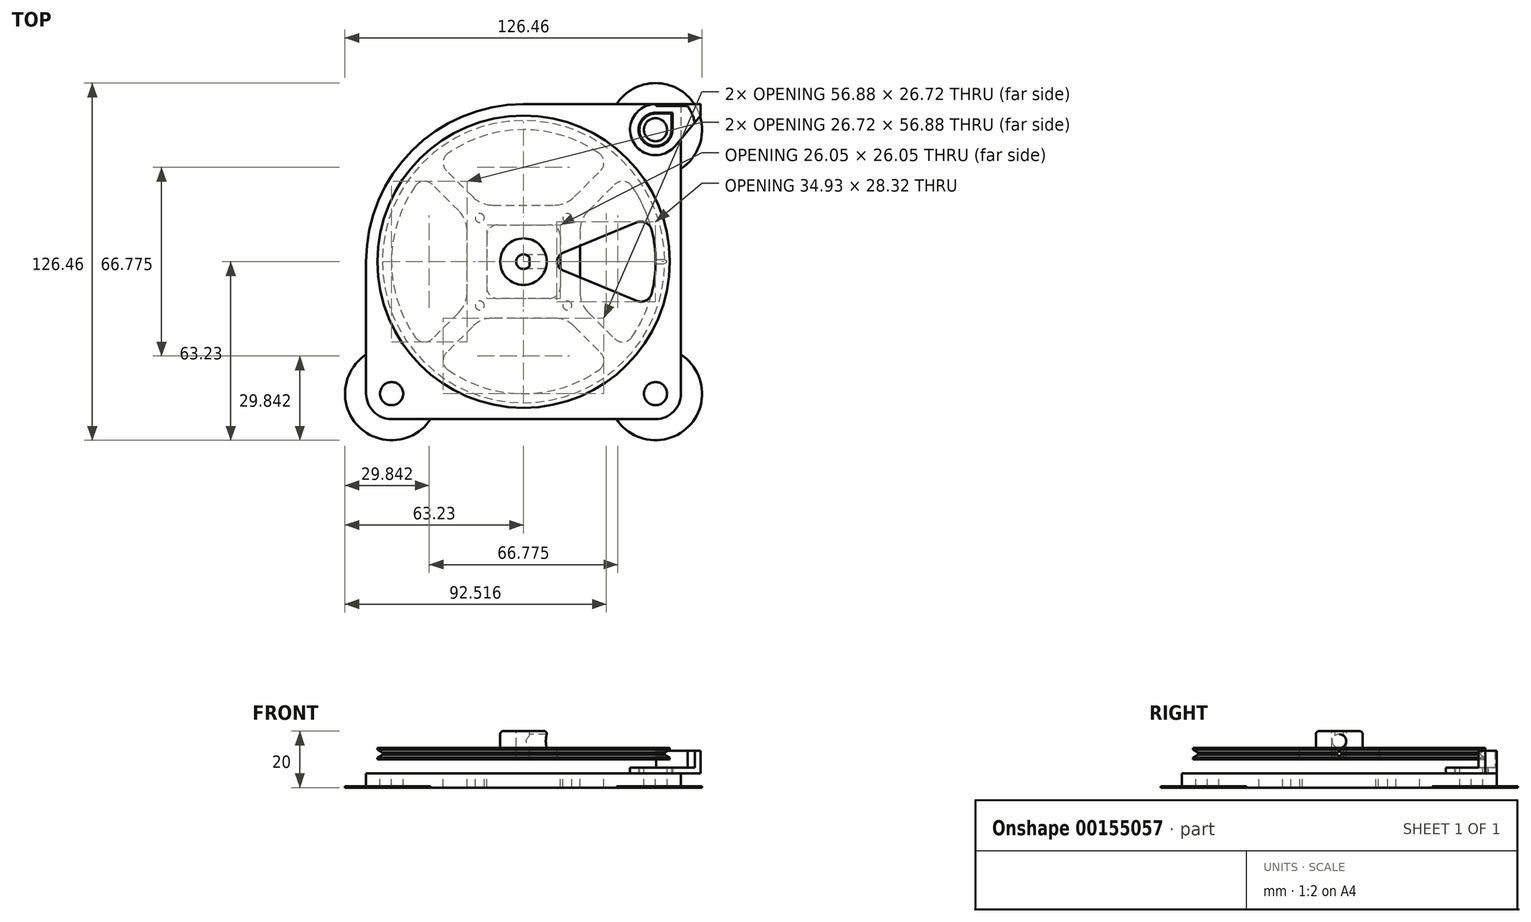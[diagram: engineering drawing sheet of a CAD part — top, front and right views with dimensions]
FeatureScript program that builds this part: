
annotation { "Feature Type Name" : "Feature", "Feature Type Description" : "" }
export const myFeature = defineFeature(function(context is Context, id is Id, definition is map)
    precondition{}
    {
        {
            var Q0;
            Q0=qCreatedBy(makeId("Top.planeOp"),FACE);
            var sketch = newSketch(context, id + "F0", { "sketchPlane" : qUnion([Q0])});
            skCircle(sketch, "E0", {"center": v(0, 0) * mm, "radius": 51.75 * mm});
            skSolve(sketch);
        }
        {
            var Q0;
            Q0 = qSketchRegion(id + "F0", true);
            extrude(context, id + "F1", {"entities" : qUnion([Q0]), "depth" : 4 * mm});
        }
        {
            var Q0;
            Q0=qCreatedBy(makeId("Front.planeOp"),FACE);
            var sketch = newSketch(context, id + "F2", { "sketchPlane" : qUnion([Q0])});
            skPoint(sketch, "E1", {"position": v(35.4, 14.63) * mm});
            skLineSegment(sketch, "E2", {"start": v(51.75, 3.4) * mm, "end": v(51.75, 0.6) * mm});
            skLineSegment(sketch, "E3", {"start": v(51.75, 3.4) * mm, "end": v(51.75, 0.6) * mm, "construction": true});
            skPoint(sketch, "E4", {"position": v(51.75, 2) * mm});
            skLineSegment(sketch, "E5", {"start": v(51.75, 3.4) * mm, "end": v(50, 2.39) * mm});
            skLineSegment(sketch, "E6", {"start": v(50, 2.39) * mm, "end": v(50, 1.61) * mm});
            skLineSegment(sketch, "E7", {"start": v(50, 1.61) * mm, "end": v(51.75, 0.6) * mm});
            skLineSegment(sketch, "E8", {"start": v(51.75, 0.6) * mm, "end": v(51.75, 3.4) * mm});
            skPoint(sketch, "E9", {"position": v(50, 2) * mm});
            skPoint(sketch, "E10.orphan", {"position": v(51.75, 4) * mm});
            skPoint(sketch, "E11.orphan", {"position": v(51.75, 0) * mm});
            skSolve(sketch);
        }
        {
            var Q0;
            Q0 = qSketchRegion(id + "F2", true);
            var Q1;
            Q1=makeQuery(id+"F1.opExtrude","CAP_EDGE",EDGE,{"disambiguationData":[OSD([sQuery(id+"F0.wireOp",EDGE,"E0")])],"isStart":false});
            revolve(context, id + "F3", {"operationType" : NewBodyOperationType.REMOVE, "entities" : qUnion([Q0]), "axis" : qUnion([Q1]), "revolveType" : RevolveType.FULL, "oppositeDirection" : true});
        }
        {
            var Q0;
            Q0=qCreatedBy(makeId("Top.planeOp"),FACE);
            var sketch = newSketch(context, id + "F4", { "sketchPlane" : qUnion([Q0])});
            skArc(sketch, "E12", {"start": v(2.09, 1.55) * mm, "mid": v(-2.6, 0) * mm, "end": v(2.09, -1.55) * mm});
            skLineSegment(sketch, "E13", {"start": v(2.1, 1.55) * mm, "end": v(2.1, -1.55) * mm});
            skSolve(sketch);
        }
        {
            var Q0;
            Q0=makeQuery(id+"F1.opExtrude","CAP_FACE",FACE,{"disambiguationData":[OSD([sQuery(id+"F0.wireOp",EDGE,"E0")])],"isStart":false});
            var sketch = newSketch(context, id + "F5", { "sketchPlane" : qUnion([Q0])});
            skArc(sketch, "E14", {"start": v(13.85, 3.03) * mm, "mid": v(11.82, 0) * mm, "end": v(13.85, -3.03) * mm});
            skLineSegment(sketch, "E15", {"start": v(13.85, 3.03) * mm, "end": v(40, 13.86) * mm});
            skLineSegment(sketch, "E16", {"start": v(13.85, -3.03) * mm, "end": v(40, -13.86) * mm});
            skLineSegment(sketch, "E17", {"start": v(0, 0) * mm, "end": v(33.6, 13.92) * mm, "construction": true});
            skArc(sketch, "E18", {"start": v(45.4, -11.12) * mm, "mid": v(46.75, 0) * mm, "end": v(45.4, 11.12) * mm});
            skPoint(sketch, "E19.visualSharp", {"position": v(44.09, 15.56) * mm});
            skArc(sketch, "E19.filletArc", {"start": v(45.4, 11.12) * mm, "mid": v(43.33, 13.73) * mm, "end": v(40, 13.86) * mm});
            skPoint(sketch, "E20.visualSharp", {"position": v(44.09, -15.56) * mm});
            skArc(sketch, "E20.filletArc", {"start": v(40, -13.86) * mm, "mid": v(43.33, -13.73) * mm, "end": v(45.4, -11.12) * mm});
            skSolve(sketch);
        }
        {
            var Q0;
            Q0 = qSketchRegion(id + "F5", true);
            extrude(context, id + "F6", {"entities" : qUnion([Q0]), "operationType" : NewBodyOperationType.REMOVE, "endBound" : BoundingType.SYMMETRIC, "depth" : 25 * mm});
        }
        {
            var Q0;
            Q0 = qSketchRegion(id + "F4", true);
            extrude(context, id + "F7", {"entities" : qUnion([Q0]), "operationType" : NewBodyOperationType.REMOVE, "endBound" : BoundingType.SYMMETRIC, "oppositeDirection" : true, "depth" : 25 * mm});
        }
        {
            var Q0;
            Q0=makeQuery(id+"F1.opExtrude","CAP_FACE",FACE,{"disambiguationData":[OSD([sQuery(id+"F0.wireOp",EDGE,"E0")])],"isStart":false});
            var sketch = newSketch(context, id + "F8", { "sketchPlane" : qUnion([Q0])});
            skCircle(sketch, "E21", {"center": v(0, 0) * mm, "radius": 8.25 * mm});
            skArc(sketch, "E22.0", {"start": v(2.09, 1.55) * mm, "mid": v(-2.6, 0) * mm, "end": v(2.09, -1.55) * mm});
            skLineSegment(sketch, "E23.0", {"start": v(2.1, 1.55) * mm, "end": v(2.1, -1.55) * mm});
            skSolve(sketch);
        }
        {
            var Q0;
            Q0 = qSketchRegion(id + "F8", true);
            extrude(context, id + "F9", {"entities" : qUnion([Q0]), "operationType" : NewBodyOperationType.ADD, "depth" : 6 * mm});
        }
        {
            var Q0;
            Q0=makeQuery(id+"F9.opExtrude","CAP_EDGE",EDGE,{"disambiguationData":[OSD([sQuery(id+"F8.wireOp",EDGE,"E21")])],"isStart":true});
            var Q1;
            Q1=makeQuery(id+"F9.opExtrude","CAP_EDGE",EDGE,{"disambiguationData":[OSD([sQuery(id+"F8.wireOp",EDGE,"E21")])],"isStart":false});
            fillet(context, id + "F10", {"entities" : qUnion([Q0, Q1]), "radius" : 1 * mm, "tangentPropagation" : true, "allowEdgeOverflow" : false});
        }
        {
            var Q0;
            Q0=qCreatedBy(makeId("Right.planeOp"),FACE);
            var sketch = newSketch(context, id + "F11", { "sketchPlane" : qUnion([Q0])});
            skCircle(sketch, "E24", {"center": v(0, 6.45) * mm, "radius": 2.45 * mm});
            skLineSegment(sketch, "E25", {"start": v(-8.25, 5.5) * mm, "end": v(-8.25, 7.4) * mm, "construction": true});
            skLineSegment(sketch, "E26", {"start": v(8.25, 8.5) * mm, "end": v(8.25, 5.5) * mm});
            skPoint(sketch, "E27", {"position": v(-8.25, 6.45) * mm});
            skSolve(sketch);
        }
        {
            var Q0;
            Q0 = qSketchRegion(id + "F11", true);
            extrude(context, id + "F12", {"entities" : qUnion([Q0]), "operationType" : NewBodyOperationType.REMOVE, "depth" : 25 * mm});
        }
        {
            var Q0;
            Q0=qCreatedBy(makeId("Right.planeOp"),FACE);
            var Q1;
            Q1=sQuery(id+"F2.wireOp",VERTEX,"E4");
            cPlane(context, id + "F13", {"entities" : qUnion([Q0, Q1]), "cplaneType" : CPlaneType.PLANE_POINT, "offset" : 25 * mm, "width" : 150 * mm, "height" : 150 * mm});
        }
        {
            var Q0;
            Q0=qCreatedBy(id+"F13.planeOp",FACE);
            var sketch = newSketch(context, id + "F14", { "sketchPlane" : qUnion([Q0])});
            skPoint(sketch, "E28.0", {"position": v(0, 2) * mm});
            skCircle(sketch, "E29", {"center": v(0, 2) * mm, "radius": 0.75 * mm});
            skSolve(sketch);
        }
        {
            var Q0;
            Q0 = qSketchRegion(id + "F14", true);
            var Q1;
            Q1=makeQuery(id+"F6.boolean.opBoolean","COPY",FACE,{"derivedFrom":makeQuery(id+"F6.opExtrude","SWEPT_FACE",FACE,{"disambiguationData":[OSD([sQuery(id+"F5.wireOp",EDGE,"E18")])]})});
            extrude(context, id + "F15", {"entities" : qUnion([Q0]), "operationType" : NewBodyOperationType.REMOVE, "endBound" : BoundingType.UP_TO_SURFACE, "oppositeDirection" : true, "endBoundEntityFace" : qUnion([Q1]), "depth" : 25 * mm});
        }
        {
            var Q0;
            Q0=qCreatedBy(makeId("Top.planeOp"),FACE);
            cPlane(context, id + "F16", {"entities" : qUnion([Q0]), "cplaneType" : CPlaneType.OFFSET, "offset" : 5 * mm, "oppositeDirection" : true, "width" : 150 * mm, "height" : 150 * mm});
        }
        {
            var Q0;
            Q0=qCreatedBy(id+"F16.planeOp",FACE);
            var sketch = newSketch(context, id + "F17", { "sketchPlane" : qUnion([Q0])});
            skArc(sketch, "E30.0", {"start": v(2.09, 1.55) * mm, "mid": v(-2.6, 0) * mm, "end": v(2.09, -1.55) * mm});
            skCircle(sketch, "E31", {"center": v(0, 0) * mm, "radius": 2.8 * mm});
            skLineSegment(sketch, "E32.bottom", {"start": v(0, 55.75) * mm, "end": v(46.73, 55.75) * mm});
            skLineSegment(sketch, "E32.top", {"start": v(-46.73, -55.75) * mm, "end": v(46.73, -55.75) * mm});
            skLineSegment(sketch, "E32.left", {"start": v(-55.75, 0) * mm, "end": v(-55.75, -46.73) * mm});
            skLineSegment(sketch, "E32.right", {"start": v(55.75, 55.75) * mm, "end": v(55.75, -46.73) * mm});
            skCircle(sketch, "E33.0", {"center": v(0, 0) * mm, "radius": 51.75 * mm, "construction": true});
            skPoint(sketch, "E34", {"position": v(-55.75, 0) * mm});
            skPoint(sketch, "E35", {"position": v(0, -55.75) * mm});
            skCircle(sketch, "E36", {"center": v(-46.73, -46.73) * mm, "radius": 4.1 * mm});
            skArc(sketch, "E37", {"start": v(-55.75, -46.73) * mm, "mid": v(-53.1, -53.1) * mm, "end": v(-46.73, -55.75) * mm});
            skArc(sketch, "E38.1.0.0", {"start": v(46.73, -55.75) * mm, "mid": v(53.1, -53.1) * mm, "end": v(55.75, -46.73) * mm});
            skCircle(sketch, "E38.1.0.1", {"center": v(46.73, -46.73) * mm, "radius": 4.1 * mm});
            skLineSegment(sketch, "E38.direction1", {"start": v(-46.73, -46.73) * mm, "end": v(46.73, -46.73) * mm, "construction": true});
            skArc(sketch, "E39.0.1.0", {"start": v(55.75, 46.73) * mm, "mid": v(53.1, 53.1) * mm, "end": v(46.73, 55.75) * mm, "construction": true});
            skCircle(sketch, "E39.0.1.1", {"center": v(46.73, 46.73) * mm, "radius": 4.1 * mm});
            skLineSegment(sketch, "E39.direction2", {"start": v(46.73, -46.73) * mm, "end": v(46.73, 46.73) * mm, "construction": true});
            skPoint(sketch, "E40.orphan", {"position": v(55.75, -55.75) * mm});
            skPoint(sketch, "E41.orphan", {"position": v(-55.75, -55.75) * mm});
            skCircle(sketch, "E42", {"center": v(0, 0) * mm, "radius": 55.75 * mm});
            skPoint(sketch, "E43.orphan", {"position": v(-55.75, 55.75) * mm});
            skArc(sketch, "E44", {"start": v(58.68, 46.73) * mm, "mid": v(57.6, 51.69) * mm, "end": v(54.57, 55.75) * mm, "construction": true});
            skLineSegment(sketch, "E45", {"start": v(58.68, 46.73) * mm, "end": v(58.68, 55.75) * mm, "construction": true});
            skLineSegment(sketch, "E46.trimOffspring", {"start": v(54.57, 55.75) * mm, "end": v(58.68, 55.75) * mm, "construction": true});
            skLineSegment(sketch, "E47.bottom", {"start": v(46.73, 55.75) * mm, "end": v(55.75, 55.75) * mm});
            skLineSegment(sketch, "E47.right", {"start": v(62.68, 55.75) * mm, "end": v(62.68, 53.75) * mm, "construction": true});
            skLineSegment(sketch, "E48.trimOffspring", {"start": v(55.75, 53.75) * mm, "end": v(62.68, 53.75) * mm, "construction": true});
            skLineSegment(sketch, "E49", {"start": v(55.75, 55.75) * mm, "end": v(62.68, 55.75) * mm, "construction": true});
            skSolve(sketch);
        }
        {
            var Q0;
            Q0 = qSketchRegion(id + "F17", true);
            extrude(context, id + "F18", {"entities" : qUnion([Q0]), "oppositeDirection" : true, "depth" : 5 * mm});
        }
        {
            var Q0;
            Q0=makeQuery(id+"F18.opExtrude","CAP_FACE",FACE,{"disambiguationData":[OSD([sQuery(id+"F17.wireOp",EDGE,"E31"),sQuery(id+"F17.wireOp",EDGE,"E32.bottom"),sQuery(id+"F17.wireOp",EDGE,"E32.top"),sQuery(id+"F17.wireOp",EDGE,"E32.left"),sQuery(id+"F17.wireOp",EDGE,"E32.right"),sQuery(id+"F17.wireOp",EDGE,"E36"),sQuery(id+"F17.wireOp",EDGE,"E37"),sQuery(id+"F17.wireOp",EDGE,"E38.1.0.0"),sQuery(id+"F17.wireOp",EDGE,"E38.1.0.1"),sQuery(id+"F17.wireOp",EDGE,"E39.0.1.0"),sQuery(id+"F17.wireOp",EDGE,"E39.0.1.1"),sQuery(id+"F17.wireOp",EDGE,"E42")])],"isStart":true});
            var sketch = newSketch(context, id + "F19", { "sketchPlane" : qUnion([Q0])});
            skLineSegment(sketch, "E50.bottom", {"start": v(-21.5, 21.75) * mm, "end": v(21.5, 21.75) * mm, "construction": true});
            skLineSegment(sketch, "E50.top", {"start": v(-21.5, -21.75) * mm, "end": v(21.5, -21.75) * mm, "construction": true});
            skLineSegment(sketch, "E50.left", {"start": v(-21.5, 21.75) * mm, "end": v(-21.5, -21.75) * mm, "construction": true});
            skLineSegment(sketch, "E50.right", {"start": v(21.5, 21.75) * mm, "end": v(21.5, -21.75) * mm, "construction": true});
            skLineSegment(sketch, "E51.bottom", {"start": v(-15.5, 15.5) * mm, "end": v(15.5, 15.5) * mm, "construction": true});
            skLineSegment(sketch, "E51.top", {"start": v(-15.5, -15.5) * mm, "end": v(15.5, -15.5) * mm, "construction": true});
            skLineSegment(sketch, "E51.left", {"start": v(-15.5, 15.5) * mm, "end": v(-15.5, -15.5) * mm, "construction": true});
            skLineSegment(sketch, "E51.right", {"start": v(15.5, 15.5) * mm, "end": v(15.5, -15.5) * mm, "construction": true});
            skPoint(sketch, "E52", {"position": v(-21.5, 0) * mm});
            skPoint(sketch, "E53", {"position": v(-15.5, 0) * mm});
            skPoint(sketch, "E54", {"position": v(0, 15.5) * mm});
            skPoint(sketch, "E55", {"position": v(0, 21.75) * mm});
            skCircle(sketch, "E56", {"center": v(-15.5, 15.5) * mm, "radius": 1.6 * mm});
            skCircle(sketch, "E57", {"center": v(15.5, -15.5) * mm, "radius": 1.6 * mm});
            skPoint(sketch, "E58", {"position": v(0, 0) * mm});
            skCircle(sketch, "E59", {"center": v(15.5, 15.5) * mm, "radius": 1.6 * mm});
            skCircle(sketch, "E60", {"center": v(-15.5, -15.5) * mm, "radius": 1.6 * mm});
            skSolve(sketch);
        }
        {
            var Q0;
            Q0 = qSketchRegion(id + "F19", true);
            extrude(context, id + "F20", {"entities" : qUnion([Q0]), "operationType" : NewBodyOperationType.REMOVE, "oppositeDirection" : true, "depth" : 25 * mm});
        }
        {
            var Q0;
            Q0=makeQuery(id+"F18.opExtrude","CAP_FACE",FACE,{"disambiguationData":[OSD([sQuery(id+"F17.wireOp",EDGE,"E31"),sQuery(id+"F17.wireOp",EDGE,"E32.bottom"),sQuery(id+"F17.wireOp",EDGE,"E32.top"),sQuery(id+"F17.wireOp",EDGE,"E32.left"),sQuery(id+"F17.wireOp",EDGE,"E32.right"),sQuery(id+"F17.wireOp",EDGE,"E36"),sQuery(id+"F17.wireOp",EDGE,"E37"),sQuery(id+"F17.wireOp",EDGE,"E38.1.0.0"),sQuery(id+"F17.wireOp",EDGE,"E38.1.0.1"),sQuery(id+"F17.wireOp",EDGE,"E39.0.1.0"),sQuery(id+"F17.wireOp",EDGE,"E39.0.1.1"),sQuery(id+"F17.wireOp",EDGE,"E42")])],"isStart":true});
            var sketch = newSketch(context, id + "F21", { "sketchPlane" : qUnion([Q0])});
            skLineSegment(sketch, "E61", {"start": v(-17.97, 13.03) * mm, "end": v(-35.44, 30.49) * mm});
            skLineSegment(sketch, "E62", {"start": v(-13.03, 17.97) * mm, "end": v(-30.49, 35.44) * mm});
            skArc(sketch, "E63.converted", {"start": v(-30.49, 35.44) * mm, "mid": v(0, 46.75) * mm, "end": v(30.49, 35.44) * mm});
            skLineSegment(sketch, "E64", {"start": v(13.03, 17.97) * mm, "end": v(30.49, 35.44) * mm});
            skLineSegment(sketch, "E65", {"start": v(17.97, 13.03) * mm, "end": v(35.44, 30.49) * mm});
            skLineSegment(sketch, "E66", {"start": v(-17.97, -13.03) * mm, "end": v(-35.44, -30.49) * mm});
            skLineSegment(sketch, "E67", {"start": v(13.03, -17.97) * mm, "end": v(30.49, -35.44) * mm});
            skLineSegment(sketch, "E68", {"start": v(17.97, -13.03) * mm, "end": v(35.44, -30.49) * mm});
            skLineSegment(sketch, "E69", {"start": v(-13.03, -17.97) * mm, "end": v(-30.49, -35.44) * mm});
            skArc(sketch, "E70.trimOffspring", {"start": v(30.49, -35.44) * mm, "mid": v(0, -46.75) * mm, "end": v(-30.49, -35.44) * mm});
            skArc(sketch, "E71.trimOffspring", {"start": v(-35.44, -30.49) * mm, "mid": v(-46.75, 0) * mm, "end": v(-35.44, 30.49) * mm});
            skArc(sketch, "E72.trimOffspring", {"start": v(35.44, 30.49) * mm, "mid": v(46.75, 0) * mm, "end": v(35.44, -30.49) * mm});
            skPoint(sketch, "E73.center.orphan", {"position": v(-15.5, -15.5) * mm});
            skPoint(sketch, "E74.center.orphan", {"position": v(15.5, -15.5) * mm});
            skPoint(sketch, "E75.center.orphan", {"position": v(15.5, 15.5) * mm});
            skCircle(sketch, "E76.0", {"center": v(-15.5, 15.5) * mm, "radius": 1.6 * mm});
            skCircle(sketch, "E77.0", {"center": v(15.5, 15.5) * mm, "radius": 1.6 * mm});
            skCircle(sketch, "E78.0", {"center": v(-15.5, -15.5) * mm, "radius": 1.6 * mm});
            skCircle(sketch, "E78.1", {"center": v(15.5, -15.5) * mm, "radius": 1.6 * mm});
            skCircle(sketch, "E79", {"center": v(-15.5, 15.5) * mm, "radius": 3.5 * mm, "construction": true});
            skCircle(sketch, "E80", {"center": v(15.5, 15.5) * mm, "radius": 3.5 * mm, "construction": true});
            skCircle(sketch, "E81", {"center": v(15.5, -15.5) * mm, "radius": 3.5 * mm, "construction": true});
            skCircle(sketch, "E82", {"center": v(-15.5, -15.5) * mm, "radius": 3.5 * mm, "construction": true});
            skLineSegment(sketch, "E83", {"start": v(-30.49, 35.44) * mm, "end": v(-13.03, 17.97) * mm, "construction": true});
            skPoint(sketch, "E84.0.start.orphan", {"position": v(-21.5, 21.75) * mm});
            skPoint(sketch, "E85.orphan", {"position": v(21.5, 21.75) * mm});
            skPoint(sketch, "E86.orphan", {"position": v(21.5, -21.75) * mm});
            skPoint(sketch, "E87.orphan", {"position": v(-21.5, -21.75) * mm});
            skCircle(sketch, "E88", {"center": v(0, 0) * mm, "radius": 18.42 * mm, "construction": true});
            skPoint(sketch, "E89", {"position": v(-13.03, 13.03) * mm});
            skPoint(sketch, "E90", {"position": v(13.03, 13.03) * mm});
            skPoint(sketch, "E91", {"position": v(13.03, -13.03) * mm});
            skPoint(sketch, "E92", {"position": v(-13.03, -13.03) * mm});
            skLineSegment(sketch, "E93", {"start": v(-13.03, 13.03) * mm, "end": v(13.03, 13.03) * mm});
            skLineSegment(sketch, "E94", {"start": v(13.03, 13.03) * mm, "end": v(13.03, -13.03) * mm});
            skLineSegment(sketch, "E95", {"start": v(13.03, -13.03) * mm, "end": v(-13.03, -13.03) * mm});
            skLineSegment(sketch, "E96", {"start": v(-13.03, 13.03) * mm, "end": v(-13.03, -13.03) * mm});
            skLineSegment(sketch, "E97", {"start": v(-15.08, 20.03) * mm, "end": v(15.08, 20.03) * mm});
            skLineSegment(sketch, "E98", {"start": v(20.03, 15.08) * mm, "end": v(20.03, -15.08) * mm});
            skLineSegment(sketch, "E99", {"start": v(15.08, -20.03) * mm, "end": v(-15.08, -20.03) * mm});
            skLineSegment(sketch, "E100", {"start": v(-20.03, -15.08) * mm, "end": v(-20.03, 15.08) * mm});
            skSolve(sketch);
        }
        {
            var Q0;
            Q0 = qSketchRegion(id + "F21", true);
            extrude(context, id + "F22", {"entities" : qUnion([Q0]), "operationType" : NewBodyOperationType.REMOVE, "endBound" : BoundingType.THROUGH_ALL, "oppositeDirection" : true, "depth" : 25 * mm});
        }
        {
            var Q0;
            Q0=makeQuery(id+"F19.imprint","IMPRINT",FACE,{"disambiguationData":[TD([[makeQuery(id+"F19.imprint","IMPRINT",EDGE,{"derivedFrom":sQuery(id+"F19.wireOp",EDGE,"E56")}),-1.0]])]});
            var sketch = newSketch(context, id + "F23", { "sketchPlane" : qUnion([Q0])});
            skCircle(sketch, "E101.0", {"center": v(46.73, 46.73) * mm, "radius": 4.1 * mm});
            skCircle(sketch, "E102", {"center": v(46.73, 46.73) * mm, "radius": 5.7 * mm});
            skPoint(sketch, "E103.0", {"position": v(55.75, 55.75) * mm});
            skLineSegment(sketch, "E104", {"start": v(55.75, 55.75) * mm, "end": v(46.73, 46.73) * mm, "construction": true});
            skLineSegment(sketch, "E105", {"start": v(46.73, 52.43) * mm, "end": v(52.43, 52.43) * mm});
            skLineSegment(sketch, "E106", {"start": v(52.43, 52.43) * mm, "end": v(52.43, 46.73) * mm});
            skSolve(sketch);
        }
        {
            var Q0;
            Q0 = qSketchRegion(id + "F23", true);
            extrude(context, id + "F24", {"entities" : qUnion([Q0]), "operationType" : NewBodyOperationType.ADD, "depth" : 2 * mm});
        }
        {
            var Q0;
            Q0=makeQuery(id+"F18.opExtrude","CAP_FACE",FACE,{"disambiguationData":[OSD([sQuery(id+"F17.wireOp",EDGE,"E31"),sQuery(id+"F17.wireOp",EDGE,"E32.bottom"),sQuery(id+"F17.wireOp",EDGE,"E32.top"),sQuery(id+"F17.wireOp",EDGE,"E32.left"),sQuery(id+"F17.wireOp",EDGE,"E32.right"),sQuery(id+"F17.wireOp",EDGE,"E36"),sQuery(id+"F17.wireOp",EDGE,"E37"),sQuery(id+"F17.wireOp",EDGE,"E38.1.0.0"),sQuery(id+"F17.wireOp",EDGE,"E38.1.0.1"),sQuery(id+"F17.wireOp",EDGE,"E39.0.1.1"),sQuery(id+"F17.wireOp",EDGE,"E42"),sQuery(id+"F17.wireOp",EDGE,"E47.bottom"),sQuery(id+"F17.wireOp",EDGE,"E47.top"),sQuery(id+"F17.wireOp",EDGE,"E47.right")])],"isStart":false});
            var sketch = newSketch(context, id + "F25", { "sketchPlane" : qUnion([Q0])});
            skCircle(sketch, "E107", {"center": v(-46.73, 46.73) * mm, "radius": 16.5 * mm});
            skCircle(sketch, "E108", {"center": v(46.73, 46.73) * mm, "radius": 16.5 * mm});
            skCircle(sketch, "E109", {"center": v(46.73, -46.73) * mm, "radius": 16.5 * mm});
            skCircle(sketch, "E110.0", {"center": v(-46.73, 46.73) * mm, "radius": 4.1 * mm});
            skCircle(sketch, "E111.0", {"center": v(46.73, 46.73) * mm, "radius": 4.1 * mm});
            skCircle(sketch, "E112.0", {"center": v(46.73, -46.73) * mm, "radius": 4.1 * mm});
            skSolve(sketch);
        }
        {
            var Q0;
            Q0 = qSketchRegion(id + "F25", true);
            extrude(context, id + "F26", {"entities" : qUnion([Q0]), "operationType" : NewBodyOperationType.ADD, "oppositeDirection" : true, "depth" : 0.5 * mm});
        }
        {
            var Q0;
            Q0=makeQuery(id+"F22.boolean.opBoolean","COPY",EDGE,{"derivedFrom":makeQuery(id+"F22.opExtrude","SWEPT_EDGE",EDGE,{"disambiguationData":[OSD([sQuery(id+"F21.wireOp",EDGE,"E66"),sQuery(id+"F21.wireOp",EDGE,"E71.trimOffspring")])]})});
            var Q1;
            Q1=makeQuery(id+"F22.boolean.opBoolean","COPY",EDGE,{"derivedFrom":makeQuery(id+"F22.opExtrude","SWEPT_EDGE",EDGE,{"disambiguationData":[OSD([sQuery(id+"F21.wireOp",EDGE,"E62"),sQuery(id+"F21.wireOp",EDGE,"E63.converted")])]})});
            var Q2;
            Q2=makeQuery(id+"F22.boolean.opBoolean","COPY",EDGE,{"derivedFrom":makeQuery(id+"F22.opExtrude","SWEPT_EDGE",EDGE,{"disambiguationData":[OSD([sQuery(id+"F21.wireOp",EDGE,"E63.converted"),sQuery(id+"F21.wireOp",EDGE,"E64")])]})});
            var Q3;
            Q3=makeQuery(id+"F22.boolean.opBoolean","COPY",EDGE,{"derivedFrom":makeQuery(id+"F22.opExtrude","SWEPT_EDGE",EDGE,{"disambiguationData":[OSD([sQuery(id+"F21.wireOp",EDGE,"E65"),sQuery(id+"F21.wireOp",EDGE,"E72.trimOffspring")])]})});
            var Q4;
            Q4=makeQuery(id+"F22.boolean.opBoolean","COPY",EDGE,{"derivedFrom":makeQuery(id+"F22.opExtrude","SWEPT_EDGE",EDGE,{"disambiguationData":[OSD([sQuery(id+"F21.wireOp",EDGE,"E61"),sQuery(id+"F21.wireOp",EDGE,"E71.trimOffspring")])]})});
            var Q5;
            Q5=makeQuery(id+"F22.boolean.opBoolean","COPY",EDGE,{"derivedFrom":makeQuery(id+"F22.opExtrude","SWEPT_EDGE",EDGE,{"disambiguationData":[OSD([sQuery(id+"F21.wireOp",EDGE,"E68"),sQuery(id+"F21.wireOp",EDGE,"E72.trimOffspring")])]})});
            var Q6;
            Q6=makeQuery(id+"F22.boolean.opBoolean","COPY",EDGE,{"derivedFrom":makeQuery(id+"F22.opExtrude","SWEPT_EDGE",EDGE,{"disambiguationData":[OSD([sQuery(id+"F21.wireOp",EDGE,"E67"),sQuery(id+"F21.wireOp",EDGE,"E70.trimOffspring")])]})});
            var Q7;
            Q7=makeQuery(id+"F22.boolean.opBoolean","COPY",EDGE,{"derivedFrom":makeQuery(id+"F22.opExtrude","SWEPT_EDGE",EDGE,{"disambiguationData":[OSD([sQuery(id+"F21.wireOp",EDGE,"E67"),sQuery(id+"F21.wireOp",EDGE,"E70.trimOffspring")])]})});
            var Q8;
            Q8=makeQuery(id+"F22.boolean.opBoolean","COPY",EDGE,{"derivedFrom":makeQuery(id+"F22.opExtrude","SWEPT_EDGE",EDGE,{"disambiguationData":[OSD([sQuery(id+"F21.wireOp",EDGE,"E68"),sQuery(id+"F21.wireOp",EDGE,"E72.trimOffspring")])]})});
            var Q9;
            Q9=makeQuery(id+"F22.boolean.opBoolean","COPY",EDGE,{"derivedFrom":makeQuery(id+"F22.opExtrude","SWEPT_EDGE",EDGE,{"disambiguationData":[OSD([sQuery(id+"F21.wireOp",EDGE,"E65"),sQuery(id+"F21.wireOp",EDGE,"E72.trimOffspring")])]})});
            var Q10;
            Q10=makeQuery(id+"F22.boolean.opBoolean","COPY",EDGE,{"derivedFrom":makeQuery(id+"F22.opExtrude","SWEPT_EDGE",EDGE,{"disambiguationData":[OSD([sQuery(id+"F21.wireOp",EDGE,"E63.converted"),sQuery(id+"F21.wireOp",EDGE,"E64")])]})});
            var Q11;
            Q11=makeQuery(id+"F22.boolean.opBoolean","COPY",EDGE,{"derivedFrom":makeQuery(id+"F22.opExtrude","SWEPT_EDGE",EDGE,{"disambiguationData":[OSD([sQuery(id+"F21.wireOp",EDGE,"E62"),sQuery(id+"F21.wireOp",EDGE,"E63.converted")])]})});
            var Q12;
            Q12=makeQuery(id+"F22.boolean.opBoolean","COPY",EDGE,{"derivedFrom":makeQuery(id+"F22.opExtrude","SWEPT_EDGE",EDGE,{"disambiguationData":[OSD([sQuery(id+"F21.wireOp",EDGE,"E69"),sQuery(id+"F21.wireOp",EDGE,"E70.trimOffspring")])]})});
            var Q13;
            Q13=makeQuery(id+"F22.boolean.opBoolean","COPY",EDGE,{"derivedFrom":makeQuery(id+"F22.opExtrude","SWEPT_EDGE",EDGE,{"disambiguationData":[OSD([sQuery(id+"F21.wireOp",EDGE,"E69"),sQuery(id+"F21.wireOp",EDGE,"E70.trimOffspring")])]})});
            var Q14;
            Q14=makeQuery(id+"F22.boolean.opBoolean","COPY",EDGE,{"derivedFrom":makeQuery(id+"F22.opExtrude","SWEPT_EDGE",EDGE,{"disambiguationData":[OSD([sQuery(id+"F21.wireOp",EDGE,"E66"),sQuery(id+"F21.wireOp",EDGE,"E71.trimOffspring")])]})});
            var Q15;
            Q15=makeQuery(id+"F22.boolean.opBoolean","COPY",EDGE,{"derivedFrom":makeQuery(id+"F22.opExtrude","SWEPT_EDGE",EDGE,{"disambiguationData":[OSD([sQuery(id+"F21.wireOp",EDGE,"E61"),sQuery(id+"F21.wireOp",EDGE,"E71.trimOffspring")])]})});
            var Q16;
            Q16=makeQuery(id+"F22.boolean.opBoolean","COPY",EDGE,{"derivedFrom":makeQuery(id+"F22.opExtrude","SWEPT_EDGE",EDGE,{"disambiguationData":[OSD([sQuery(id+"F21.wireOp",EDGE,"E95"),sQuery(id+"F21.wireOp",EDGE,"E96")])]})});
            var Q17;
            Q17=makeQuery(id+"F22.boolean.opBoolean","COPY",EDGE,{"derivedFrom":makeQuery(id+"F22.opExtrude","SWEPT_EDGE",EDGE,{"disambiguationData":[OSD([sQuery(id+"F21.wireOp",EDGE,"E93"),sQuery(id+"F21.wireOp",EDGE,"E96")])]})});
            var Q18;
            Q18=makeQuery(id+"F22.boolean.opBoolean","COPY",EDGE,{"derivedFrom":makeQuery(id+"F22.opExtrude","SWEPT_EDGE",EDGE,{"disambiguationData":[OSD([sQuery(id+"F21.wireOp",EDGE,"E94"),sQuery(id+"F21.wireOp",EDGE,"E95")])]})});
            var Q19;
            Q19=makeQuery(id+"F22.boolean.opBoolean","COPY",EDGE,{"derivedFrom":makeQuery(id+"F22.opExtrude","SWEPT_EDGE",EDGE,{"disambiguationData":[OSD([sQuery(id+"F21.wireOp",EDGE,"E93"),sQuery(id+"F21.wireOp",EDGE,"E94")])]})});
            fillet(context, id + "F27", {"entities" : qUnion([Q0, Q1, Q2, Q3, Q4, Q5, Q6, Q7, Q8, Q9, Q10, Q11, Q12, Q13, Q14, Q15, Q16, Q17, Q18, Q19]), "radius" : 4 * mm, "tangentPropagation" : true, "allowEdgeOverflow" : false});
        }
        {
            var Q0;
            Q0=makeQuery(id+"F22.boolean.opBoolean","COPY",EDGE,{"derivedFrom":makeQuery(id+"F22.opExtrude","SWEPT_EDGE",EDGE,{"disambiguationData":[OSD([sQuery(id+"F21.wireOp",EDGE,"E69"),sQuery(id+"F21.wireOp",EDGE,"dKGzk5BT-5LgO-388H-QMJQ-iGaYZgdvuo4U")])]})});
            var Q1;
            Q1=makeQuery(id+"F22.boolean.opBoolean","COPY",EDGE,{"derivedFrom":makeQuery(id+"F22.opExtrude","SWEPT_EDGE",EDGE,{"disambiguationData":[OSD([sQuery(id+"F21.wireOp",EDGE,"E67"),sQuery(id+"F21.wireOp",EDGE,"dKGzk5BT-5LgO-388H-QMJQ-iGaYZgdvuo4U")])]})});
            var Q2;
            Q2=makeQuery(id+"F22.boolean.opBoolean","COPY",EDGE,{"derivedFrom":makeQuery(id+"F22.opExtrude","SWEPT_EDGE",EDGE,{"disambiguationData":[OSD([sQuery(id+"F21.wireOp",EDGE,"E65"),sQuery(id+"F21.wireOp",EDGE,"oJW9VzDO-LyWC-H5L1-CJFN-JLt2SU1mvD2c")])]})});
            var Q3;
            Q3=makeQuery(id+"F22.boolean.opBoolean","COPY",EDGE,{"derivedFrom":makeQuery(id+"F22.opExtrude","SWEPT_EDGE",EDGE,{"disambiguationData":[OSD([sQuery(id+"F21.wireOp",EDGE,"E68"),sQuery(id+"F21.wireOp",EDGE,"oJW9VzDO-LyWC-H5L1-CJFN-JLt2SU1mvD2c")])]})});
            var Q4;
            Q4=makeQuery(id+"F22.boolean.opBoolean","COPY",EDGE,{"derivedFrom":makeQuery(id+"F22.opExtrude","SWEPT_EDGE",EDGE,{"disambiguationData":[OSD([sQuery(id+"F21.wireOp",EDGE,"E64"),sQuery(id+"F21.wireOp",EDGE,"CYDgP7eY-oL6e-RUfk-kUfO-LZ61UPN5qcSO")])]})});
            var Q5;
            Q5=makeQuery(id+"F22.boolean.opBoolean","COPY",EDGE,{"derivedFrom":makeQuery(id+"F22.opExtrude","SWEPT_EDGE",EDGE,{"disambiguationData":[OSD([sQuery(id+"F21.wireOp",EDGE,"E62"),sQuery(id+"F21.wireOp",EDGE,"CYDgP7eY-oL6e-RUfk-kUfO-LZ61UPN5qcSO")])]})});
            var Q6;
            Q6=makeQuery(id+"F22.boolean.opBoolean","COPY",EDGE,{"derivedFrom":makeQuery(id+"F22.opExtrude","SWEPT_EDGE",EDGE,{"disambiguationData":[OSD([sQuery(id+"F21.wireOp",EDGE,"E61"),sQuery(id+"F21.wireOp",EDGE,"PSLHS1B4-CW4d-3WD9-uAXD-E0sG6PQShj1p")])]})});
            var Q7;
            Q7=makeQuery(id+"F22.boolean.opBoolean","COPY",EDGE,{"derivedFrom":makeQuery(id+"F22.opExtrude","SWEPT_EDGE",EDGE,{"disambiguationData":[OSD([sQuery(id+"F21.wireOp",EDGE,"E66"),sQuery(id+"F21.wireOp",EDGE,"PSLHS1B4-CW4d-3WD9-uAXD-E0sG6PQShj1p")])]})});
            fillet(context, id + "F28", {"entities" : qUnion([Q0, Q1, Q2, Q3, Q4, Q5, Q6, Q7]), "radius" : 10 * mm, "tangentPropagation" : true, "allowEdgeOverflow" : false});
        }
        {
            var Q0;
            {var subQ0=sQuery(id+"F23.wireOp",EDGE,"E105");Q0=makeQuery(id+"F23.imprint","IMPRINT",FACE,{"disambiguationData":[TD([[makeQuery(id+"F23.imprint","IMPRINT",EDGE,{"derivedFrom":subQ0}),1.0]])]});}
            var sketch = newSketch(context, id + "F29", { "sketchPlane" : qUnion([Q0])});
            skLineSegment(sketch, "E113.0", {"start": v(46.73, 52.43) * mm, "end": v(52.43, 52.43) * mm, "construction": true});
            skArc(sketch, "E114.0", {"start": v(46.73, 52.43) * mm, "mid": v(42.7, 42.7) * mm, "end": v(52.43, 46.73) * mm, "construction": true});
            skLineSegment(sketch, "E115.0", {"start": v(52.43, 52.43) * mm, "end": v(52.43, 46.73) * mm, "construction": true});
            skArc(sketch, "E116", {"start": v(46.73, 55.75) * mm, "mid": v(40.35, 40.35) * mm, "end": v(55.75, 46.73) * mm});
            skArc(sketch, "E117", {"start": v(46.73, 52.73) * mm, "mid": v(42.49, 42.49) * mm, "end": v(52.73, 46.73) * mm});
            skLineSegment(sketch, "E118", {"start": v(46.73, 52.73) * mm, "end": v(52.73, 52.73) * mm});
            skLineSegment(sketch, "E119", {"start": v(52.73, 52.73) * mm, "end": v(52.73, 46.73) * mm});
            skLineSegment(sketch, "E120", {"start": v(46.73, 55.75) * mm, "end": v(55.75, 55.75) * mm});
            skLineSegment(sketch, "E121", {"start": v(55.75, 55.75) * mm, "end": v(55.75, 46.73) * mm});
            skLineSegment(sketch, "E122", {"start": v(55.75, 55.75) * mm, "end": v(62.68, 55.75) * mm});
            skLineSegment(sketch, "E123", {"start": v(62.68, 55.75) * mm, "end": v(62.68, 51.72) * mm});
            skLineSegment(sketch, "E124", {"start": v(62.68, 51.72) * mm, "end": v(53.64, 40.94) * mm});
            skPoint(sketch, "E125.0", {"position": v(62.68, 55.75) * mm});
            skSolve(sketch);
        }
        {
            var Q0;
            Q0 = qSketchRegion(id + "F29", true);
            extrude(context, id + "F30", {"entities" : qUnion([Q0]), "depth" : 2 * mm});
        }
        {
            var Q0;
            Q0=makeQuery(id+"F30.opExtrude","CAP_FACE",FACE,{"disambiguationData":[OSD([sQuery(id+"F29.wireOp",EDGE,"E116"),sQuery(id+"F29.wireOp",EDGE,"E117"),sQuery(id+"F29.wireOp",EDGE,"E118"),sQuery(id+"F29.wireOp",EDGE,"E119"),sQuery(id+"F29.wireOp",EDGE,"E120"),sQuery(id+"F29.wireOp",EDGE,"E121")])],"isStart":false});
            var sketch = newSketch(context, id + "F31", { "sketchPlane" : qUnion([Q0])});
            skArc(sketch, "E126.0", {"start": v(46.73, 55.75) * mm, "mid": v(38.56, 42.92) * mm, "end": v(53.64, 40.94) * mm});
            skLineSegment(sketch, "E127.0", {"start": v(53.64, 55.75) * mm, "end": v(53.64, 40.94) * mm});
            skLineSegment(sketch, "E128.0", {"start": v(46.73, 55.75) * mm, "end": v(53.64, 55.75) * mm});
            skCircle(sketch, "E129.0", {"center": v(46.73, 46.73) * mm, "radius": 4.1 * mm});
            skLineSegment(sketch, "E130.0", {"start": v(62.68, 51.72) * mm, "end": v(62.68, 51.72) * mm});
            skLineSegment(sketch, "E131.0", {"start": v(62.68, 55.75) * mm, "end": v(62.68, 51.72) * mm});
            skLineSegment(sketch, "E132.0", {"start": v(46.73, 55.75) * mm, "end": v(62.68, 55.75) * mm});
            skLineSegment(sketch, "E133.0", {"start": v(62.68, 51.72) * mm, "end": v(53.64, 40.94) * mm});
            skSolve(sketch);
        }
        {
            var Q0;
            {var subQ2=sQuery(id+"F31.wireOp",EDGE,"E127.0");Q0=makeQuery(id+"F31.imprint","IMPRINT",FACE,{"disambiguationData":[TD([[makeQuery(id+"F31.imprint","IMPRINT",EDGE,{"derivedFrom":subQ2}),-1.0]])]});}
            var sketch = newSketch(context, id + "F32", { "sketchPlane" : qUnion([Q0])});
            skPoint(sketch, "E134.orphan", {"position": v(55.4, 46.77) * mm});
            skLineSegment(sketch, "E135.0", {"start": v(62.68, 51.72) * mm, "end": v(53.64, 40.94) * mm, "construction": true});
            skLineSegment(sketch, "E136.0", {"start": v(46.73, 55.75) * mm, "end": v(58.68, 55.75) * mm, "construction": true});
            skLineSegment(sketch, "E137.0", {"start": v(58.68, 46.73) * mm, "end": v(58.68, 55.75) * mm, "construction": true});
            skArc(sketch, "E138.0", {"start": v(58.68, 46.73) * mm, "mid": v(57.6, 51.69) * mm, "end": v(54.57, 55.75) * mm, "construction": true});
            skArc(sketch, "E139", {"start": v(60.6, 49.24) * mm, "mid": v(59.5, 52.7) * mm, "end": v(57.57, 55.75) * mm});
            skLineSegment(sketch, "E140", {"start": v(62.68, 55.75) * mm, "end": v(58.68, 55.75) * mm});
            skLineSegment(sketch, "E141.trimOffspring", {"start": v(58.07, 55.75) * mm, "end": v(62.68, 55.75) * mm, "construction": true});
            skLineSegment(sketch, "E142.0", {"start": v(62.68, 55.75) * mm, "end": v(62.68, 51.72) * mm});
            skLineSegment(sketch, "E143", {"start": v(62.68, 51.72) * mm, "end": v(60.6, 49.24) * mm});
            skLineSegment(sketch, "E144.bottom", {"start": v(58.68, 55.75) * mm, "end": v(46.96, 55.75) * mm});
            skLineSegment(sketch, "E144.top", {"start": v(58.68, 55.12) * mm, "end": v(46.96, 55.12) * mm});
            skLineSegment(sketch, "E144.left", {"start": v(58.68, 55.75) * mm, "end": v(58.68, 55.12) * mm});
            skLineSegment(sketch, "E144.right", {"start": v(46.96, 55.75) * mm, "end": v(46.96, 55.12) * mm});
            skSolve(sketch);
        }
        {
            var Q0;
            Q0 = qSketchRegion(id + "F32", true);
            extrude(context, id + "F33", {"entities" : qUnion([Q0]), "operationType" : NewBodyOperationType.ADD, "depth" : 6 * mm});
        }
    });
